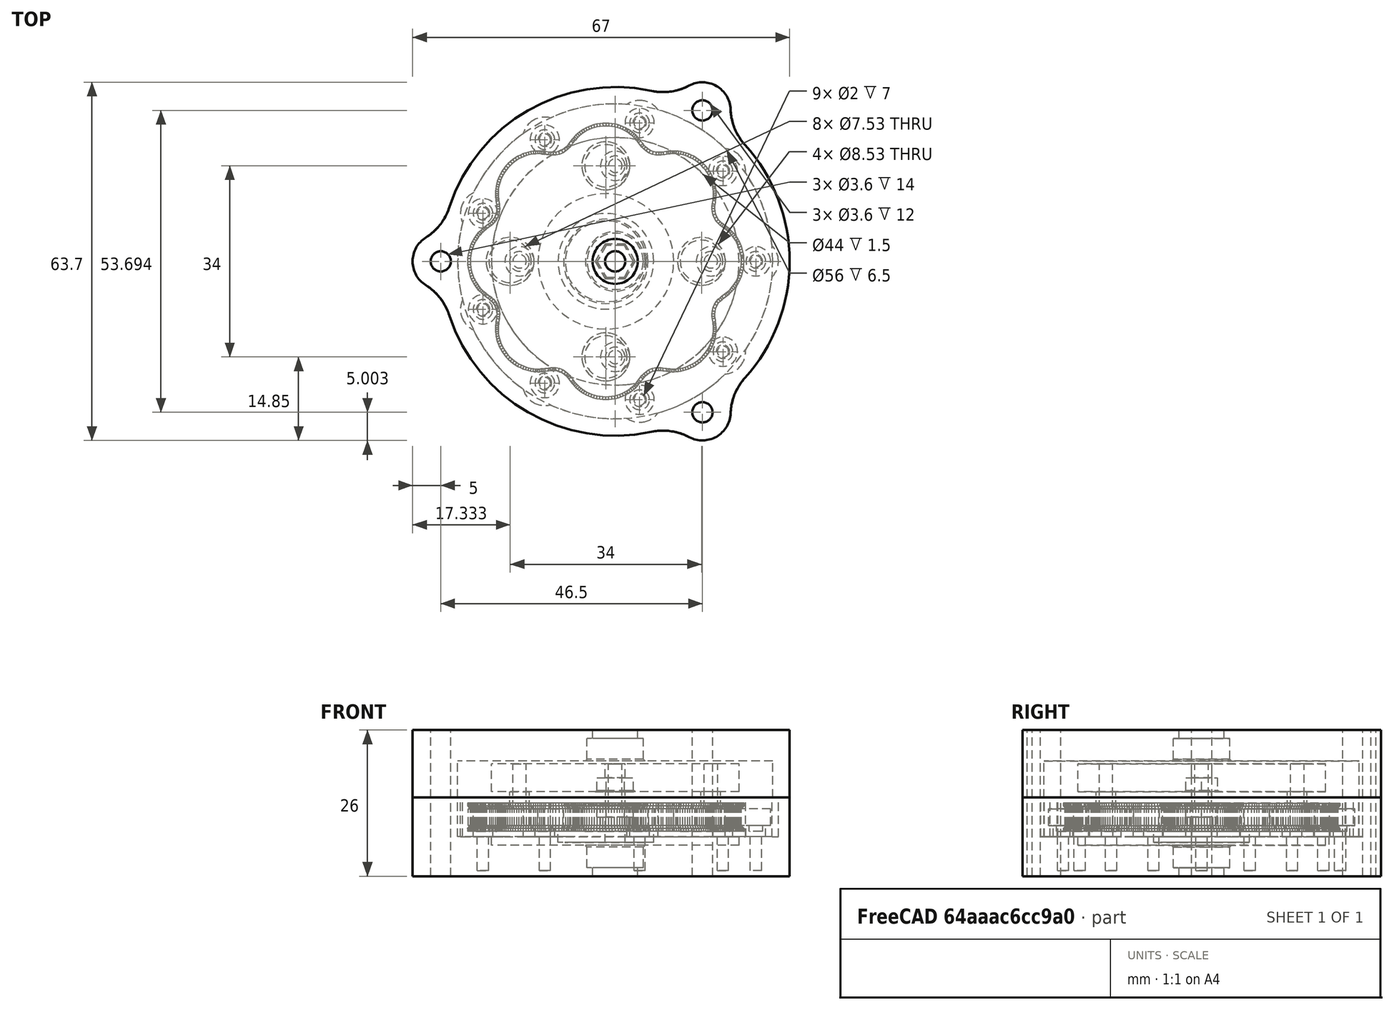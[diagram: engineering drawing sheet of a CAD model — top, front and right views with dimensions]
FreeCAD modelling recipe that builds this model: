
FCSTD DOCUMENT  (FreeCAD 0.19R24291 (Git))
Label: gearbox
License: All rights reserved
LicenseURL: http://en.wikipedia.org/wiki/All_rights_reserved
objects: Part::Feature×43, Part::Cylinder×24, Part::MultiFuse×20, Part::Cut×13, Part::Chamfer×4, Part::Box×2, Part::Fillet×2
note: 108 computed .brp shape members not serialized (recipe doc carries the construction recipe); baked Part::Feature solids carry a one-line shape summary decoded from their .brp

FEATURE [Part::Cylinder] Cylinder
  Angle = 360
  AttacherType = Attacher::AttachEngine3D
  Height = 7
  Placement = pos=(-1.6666,0,-3) rot=(0,0,1;0rad)
  Radius = 7.5
FEATURE [Part::Cylinder] Cylinder036  label="M3"
  Angle = 360
  AttacherType = Attacher::AttachEngine3D
  Height = 16
  Placement = pos=(0,0,-9) rot=(0,0,1;0rad)
  Radius = 1.8
FEATURE [Part::Cylinder] Cylinder038
  Angle = 360
  AttacherType = Attacher::AttachEngine3D
  Height = 2
  Placement = pos=(-1.66666,0,-3) rot=(0,0,1;0rad)
  Radius = 8.5
FEATURE [Part::Cylinder] Cylinder039  label="m2-tap-a"
  Angle = 360
  AttacherType = Attacher::AttachEngine3D
  Height = 30
  Placement = pos=(25,0,-1) rot=(0,0,1;0rad)
  Radius = 1.2
FEATURE [Part::Cylinder] Cylinder039009  label="m2-tap-a001"
  Angle = 360
  AttacherType = Attacher::AttachEngine3D
  Height = 30
  Placement = pos=(17,0,-8) rot=(0,0,1;0rad)
  Radius = 1.2
FEATURE [Part::Feature] Cylinder039009001
  Placement = pos=(1.9e-15,17,-8) rot=(0,0,1;1.5708rad)
  shape: bbox 2.4 x 2.4 x 30 mm, 3 faces (baked)
FEATURE [Part::Feature] Cylinder039009002
  Placement = pos=(-17,2e-15,-8) rot=(0,0,1;3.14159rad)
  shape: bbox 2.4 x 2.4 x 30 mm, 3 faces (baked)
FEATURE [Part::Feature] Cylinder039009003
  Placement = pos=(-4e-15,-17,-8) rot=(0,0,-1;1.5708rad)
  shape: bbox 2.4 x 2.4 x 30 mm, 3 faces (baked)
FEATURE [Part::MultiFuse] Fusion003  label="roller-m2-taps"
  Shapes = -> [Cylinder039009,Cylinder039009001,Cylinder039009002,Cylinder039009003]
FEATURE [Part::Feature] Shape  label="cycloid"
  Placement = pos=(-1.66667,0,0) rot=(0,0,1;0rad)
  shape: bbox 49.13 x 49.13 x 5 mm, 1823 faces (baked)
FEATURE [Part::Feature] Shape002  label="rollers"
  shape: bbox 39.2 x 39.2 x 3 mm, 12 faces, 4 solids (baked)
FEATURE [Part::Feature] Shape003  label="bearings"
  shape: bbox 53.69 x 54.44 x 3 mm, 27 faces, 9 solids (baked)
FEATURE [Part::Cylinder] Cylinder039009004
  Angle = 360
  AttacherType = Attacher::AttachEngine3D
  Height = 2
  Placement = pos=(25,0,-2) rot=(0,0,1;0rad)
  Radius = 1.75
FEATURE [Part::Feature] Cylinder039009004001
  Placement = pos=(19.1511,16.0697,-2) rot=(0,0,1;0.698132rad)
  shape: bbox 3.5 x 3.5 x 2 mm, 3 faces (baked)
FEATURE [Part::Feature] Cylinder039009004002
  Placement = pos=(4.3412,24.6202,-2) rot=(0,0,1;1.39626rad)
  shape: bbox 3.5 x 3.5 x 2 mm, 3 faces (baked)
FEATURE [Part::Feature] Cylinder039009004003
  Placement = pos=(-12.5,21.6506,-2) rot=(0,0,1;2.0944rad)
  shape: bbox 3.5 x 3.5 x 2 mm, 3 faces (baked)
FEATURE [Part::Feature] Cylinder039009004004
  Placement = pos=(-23.4923,8.5505,-2) rot=(0,0,1;2.79253rad)
  shape: bbox 3.5 x 3.5 x 2 mm, 3 faces (baked)
FEATURE [Part::Feature] Cylinder039009004005
  Placement = pos=(-23.4923,-8.5505,-2) rot=(0,0,1;3.49066rad)
  shape: bbox 3.5 x 3.5 x 2 mm, 3 faces (baked)
FEATURE [Part::Feature] Cylinder039009004006
  Placement = pos=(-12.5,-21.6506,-2) rot=(0,0,1;4.18879rad)
  shape: bbox 3.5 x 3.5 x 2 mm, 3 faces (baked)
FEATURE [Part::Feature] Cylinder039009004007
  Placement = pos=(4.3412,-24.6202,-2) rot=(0,0,-1;1.39626rad)
  shape: bbox 3.5 x 3.5 x 2 mm, 3 faces (baked)
FEATURE [Part::Feature] Cylinder039009004008
  Placement = pos=(19.1511,-16.0697,-2) rot=(0,0,-1;0.698132rad)
  shape: bbox 3.5 x 3.5 x 2 mm, 3 faces (baked)
FEATURE [Part::MultiFuse] Fusion004  label="bearing supports"
  Shapes = -> [Cylinder039009004,Cylinder039009004001,Cylinder039009004002,Cylinder039009004003,Cylinder039009004004,Cylinder039009004005,Cylinder039009004006,Cylinder039009004007,Cylinder039009004008]
FEATURE [Part::Cylinder] Cylinder039009004009
  Angle = 360
  AttacherType = Attacher::AttachEngine3D
  Height = 13
  Placement = pos=(25,0,-1) rot=(0,0,1;0rad)
  Radius = 4
FEATURE [Part::Feature] Cylinder039009004009001
  Placement = pos=(19.1511,16.0697,-1) rot=(0,0,1;0.698132rad)
  shape: bbox 8 x 8 x 13 mm, 3 faces (baked)
FEATURE [Part::Feature] Cylinder039009004009002
  Placement = pos=(4.3412,24.6202,-1) rot=(0,0,1;1.39626rad)
  shape: bbox 8 x 8 x 13 mm, 3 faces (baked)
FEATURE [Part::Feature] Cylinder039009004009003
  Placement = pos=(-12.5,21.6506,-1) rot=(0,0,1;2.0944rad)
  shape: bbox 8 x 8 x 13 mm, 3 faces (baked)
FEATURE [Part::Feature] Cylinder039009004009004
  Placement = pos=(-23.4923,8.5505,-1) rot=(0,0,1;2.79253rad)
  shape: bbox 8 x 8 x 13 mm, 3 faces (baked)
FEATURE [Part::Feature] Cylinder039009004009005
  Placement = pos=(-23.4923,-8.5505,-1) rot=(0,0,1;3.49066rad)
  shape: bbox 8 x 8 x 13 mm, 3 faces (baked)
FEATURE [Part::Feature] Cylinder039009004009006
  Placement = pos=(-12.5,-21.6506,-1) rot=(0,0,1;4.18879rad)
  shape: bbox 8 x 8 x 13 mm, 3 faces (baked)
FEATURE [Part::Feature] Cylinder039009004009007
  Placement = pos=(4.3412,-24.6202,-1) rot=(0,0,-1;1.39626rad)
  shape: bbox 8 x 8 x 13 mm, 3 faces (baked)
FEATURE [Part::Feature] Cylinder039009004009008
  Placement = pos=(19.1511,-16.0697,-1) rot=(0,0,-1;0.698132rad)
  shape: bbox 8 x 8 x 13 mm, 3 faces (baked)
FEATURE [Part::MultiFuse] Fusion005  label="bearing-cavities"
  Placement = pos=(0,0,-1) rot=(0,0,1;0rad)
  Shapes = -> [Cylinder039009004009,Cylinder039009004009001,Cylinder039009004009002,Cylinder039009004009003,Cylinder039009004009004,Cylinder039009004009005,Cylinder039009004009006,Cylinder039009004009007,Cylinder039009004009008]
FEATURE [Part::Cylinder] Cylinder039009004009009  label="case-0"
  Angle = 360
  AttacherType = Attacher::AttachEngine3D
  Height = 14
  Placement = pos=(0,0,-9) rot=(0,0,1;0rad)
  Radius = 31
FEATURE [Part::Cylinder] Cylinder039009004009010  label="case-hole-1"
  Angle = 360
  AttacherType = Attacher::AttachEngine3D
  Height = 28
  Placement = pos=(0,0,-2) rot=(0,0,1;0rad)
  Radius = 28
FEATURE [Part::Cylinder] Cylinder039009004009011  label="case-hole-2"
  Angle = 360
  AttacherType = Attacher::AttachEngine3D
  Height = 5
  Placement = pos=(0,0,-3.5) rot=(0,0,1;0rad)
  Radius = 22
FEATURE [Part::Cylinder] Cylinder039009004009012  label="output-1"
  Angle = 360
  AttacherType = Attacher::AttachEngine3D
  Height = 5
  Placement = pos=(0,0,6) rot=(0,0,1;0rad)
  Radius = 22
FEATURE [Part::Cylinder] Cylinder039009004009013
  Angle = 360
  AttacherType = Attacher::AttachEngine3D
  Height = 4
  Placement = pos=(17,0,3) rot=(0,0,1;0rad)
  Radius = 1.75
FEATURE [Part::Feature] Cylinder039009004009013001
  Placement = pos=(1.9e-15,17,3) rot=(0,0,1;1.5708rad)
  shape: bbox 3.5 x 3.5 x 4 mm, 3 faces (baked)
FEATURE [Part::Feature] Cylinder039009004009013002
  Placement = pos=(-17,2e-15,3) rot=(0,0,1;3.14159rad)
  shape: bbox 3.5 x 3.5 x 4 mm, 3 faces (baked)
FEATURE [Part::Feature] Cylinder039009004009013003
  Placement = pos=(-4e-15,-17,3) rot=(0,0,-1;1.5708rad)
  shape: bbox 3.5 x 3.5 x 4 mm, 3 faces (baked)
FEATURE [Part::MultiFuse] Fusion008  label="roller-supports"
  Shapes = -> [Cylinder039009004009013,Cylinder039009004009013001,Cylinder039009004009013002,Cylinder039009004009013003]
FEATURE [Part::MultiFuse] Fusion009  label="output-2"
  Shapes = -> [Cylinder039009004009012,Fusion008]
FEATURE [Part::Cut] Cut004  label="output-3"
  Base = -> Fusion009
  Tool = -> Fusion003
FEATURE [Part::Feature] M3_Nut_Hole
  Placement = pos=(0,0,2.5) rot=(0,0,1;0rad)
  shape: bbox 6.466 x 5.6 x 6 mm, 8 faces (baked)
FEATURE [Part::Cylinder] Cylinder039009004009013004
  Angle = 360
  AttacherType = Attacher::AttachEngine3D
  Height = 23
  Placement = pos=(0,0,3) rot=(0,0,1;0rad)
  Radius = 1.8
FEATURE [Part::MultiFuse] Fusion010  label="output-screw"
  Shapes = -> [Cylinder039009004009013004,M3_Nut_Hole]
FEATURE [Part::Cut] Cut005  label="output-4"
  Base = -> Cut004
  Tool = -> Fusion010
FEATURE [Part::Chamfer] Chamfer002  label="output"
  Base = -> Cut005
  Edges = 6 edges r=0.3: [Edge11,Edge12,Edge13,Edge14,Edge15,Edge16]
FEATURE [Part::Cylinder] Cylinder039009004009013005  label="case-hole-003"
  Angle = 360
  AttacherType = Attacher::AttachEngine3D
  Height = 13.5
  Placement = pos=(0,0,-2) rot=(0,0,1;0rad)
  Radius = 28
FEATURE [Part::Cylinder] Cylinder039009004009013006  label="case-005"
  Angle = 360
  AttacherType = Attacher::AttachEngine3D
  Height = 12
  Placement = pos=(0,0,5) rot=(0,0,1;0rad)
  Radius = 31
FEATURE [Part::Cut] Cut006  label="top-1"
  Base = -> Cylinder039009004009013006
  Tool = -> Cylinder039009004009013005
FEATURE [Part::Cylinder] Cylinder039009004009013007  label="10mm-bearing"
  Angle = 360
  AttacherType = Attacher::AttachEngine3D
  Height = 4
  Placement = pos=(0,0,11.5) rot=(0,0,1;0rad)
  Radius = 5
FEATURE [Part::Cylinder] Cylinder039009004009013008  label="output-hole"
  Angle = 360
  AttacherType = Attacher::AttachEngine3D
  Height = 10
  Placement = pos=(0,0,13) rot=(0,0,1;0rad)
  Radius = 4
FEATURE [Part::MultiFuse] Fusion011  label="output-hole-2"
  Shapes = -> [Cylinder039009004009013007,Cylinder039009004009013008]
FEATURE [Part::Cut] Cut007  label="top-3"
  Base = -> Cut006
  Tool = -> Fusion011
FEATURE [Part::Cylinder] Cylinder039009004009013009  label="case-screw-1"
  Angle = 360
  AttacherType = Attacher::AttachEngine3D
  Height = 14
  Placement = pos=(-31,0,-9) rot=(0,0,1;0rad)
  Radius = 5
FEATURE [Part::Cylinder] Cylinder039009004009013010  label="top-screw-1"
  Angle = 360
  AttacherType = Attacher::AttachEngine3D
  Height = 12
  Placement = pos=(-31,0,5) rot=(0,0,1;0rad)
  Radius = 5
FEATURE [Part::Box] Box  label="Cube"
  AttacherType = Attacher::AttachEngine3D
  Height = 56
  Length = 16
  Placement = pos=(-29,-8,-26) rot=(0,0,1;0rad)
  Width = 16
FEATURE [Part::Box] Box001  label="Cube001"
  AttacherType = Attacher::AttachEngine3D
  Height = 56
  Length = 16
  Placement = pos=(-29,-8,-26) rot=(0,0,1;0rad)
  Width = 16
FEATURE [Part::Cut] Cut008  label="case-boss-1"
  Base = -> Cylinder039009004009013009
  Tool = -> Box
FEATURE [Part::Cut] Cut009  label="top-screw-2"
  Base = -> Cylinder039009004009013010
  Tool = -> Box001
FEATURE [Part::Cylinder] Cylinder039009004009013011  label="case-screw-M3"
  Angle = 360
  AttacherType = Attacher::AttachEngine3D
  Height = 47
  Placement = pos=(-31,0,-26) rot=(0,0,1;0rad)
  Radius = 1.8
FEATURE [Part::Cylinder] Cylinder039009004009013012  label="Top-screw-clear-1"
  Angle = 360
  AttacherType = Attacher::AttachEngine3D
  Height = 47
  Placement = pos=(-31,0,-26) rot=(0,0,1;0rad)
  Radius = 1.8
FEATURE [Part::Feature] Cut009001
  Placement = pos=(0,0,0) rot=(0,0,1;2.0944rad)
  shape: bbox 9.969 x 9.023 x 12 mm, 4 faces (baked)
FEATURE [Part::Feature] Cut009002
  Placement = pos=(0,0,0) rot=(0,0,1;4.18879rad)
  shape: bbox 9.969 x 9.023 x 12 mm, 4 faces (baked)
FEATURE [Part::Feature] Cylinder039009004009013012001
  Placement = pos=(15.5,-26.8468,-26) rot=(0,0,1;2.0944rad)
  shape: bbox 3.6 x 3.6 x 47 mm, 3 faces (baked)
FEATURE [Part::Feature] Cylinder039009004009013012002
  Placement = pos=(15.5,26.8468,-26) rot=(0,0,1;4.18879rad)
  shape: bbox 3.6 x 3.6 x 47 mm, 3 faces (baked)
FEATURE [Part::MultiFuse] Fusion015  label="top-screw-clears"
  Shapes = -> [Cylinder039009004009013012,Cylinder039009004009013012001,Cylinder039009004009013012002]
FEATURE [Part::MultiFuse] Fusion016  label="top-screws"
  Shapes = -> [Cut009,Cut009001,Cut009002]
FEATURE [Part::MultiFuse] Fusion017  label="top-4"
  Shapes = -> [Cut007,Fusion016]
FEATURE [Part::Cut] Cut009006  label="top-5"
  Base = -> Fusion017
  Tool = -> Fusion015
FEATURE [Part::Fillet] Fillet001  label="top-6"
  Base = -> Cut009006
  Edges = 6 edges r=10: [Edge3,Edge6,Edge22,Edge36,Edge42,Edge47]
FEATURE [Part::Feature] M3_Nut_Hole001
  Placement = pos=(0,0,1.5) rot=(0,0,1;0rad)
  shape: bbox 6.466 x 5.6 x 6 mm, 8 faces (baked)
FEATURE [Part::MultiFuse] Fusion  label="M3-hex"
  Shapes = -> [Cylinder036,M3_Nut_Hole001]
FEATURE [Part::MultiFuse] Fusion019  label="drive-1"
  Shapes = -> [Cylinder,Cylinder038]
FEATURE [Part::Cut] Cut  label="drive-2"
  Base = -> Fusion019
  Tool = -> Fusion
FEATURE [Part::Chamfer] Chamfer  label="drive"
  Base = -> Cut
  Edges = 7 edges r=0.3: [Edge3,Edge5,Edge6,Edge7,Edge8,Edge9,Edge10]
FEATURE [Part::MultiFuse] Fusion020  label="case-hole"
  Shapes = -> [Cylinder039009004009010,Cylinder039009004009011]
FEATURE [Part::Cut] Cut009007  label="case-1"
  Base = -> Cylinder039009004009009
  Tool = -> Fusion020
FEATURE [Part::Cut] Cut009008  label="case-3"
  Base = -> Cut009007
  Tool = -> Fusion005
FEATURE [Part::MultiFuse] Fusion021  label="case-4"
  Shapes = -> [Cut009008,Fusion004]
FEATURE [Part::Cylinder] Cylinder039009004009013012003  label="m2-tap-a002"
  Angle = 360
  AttacherType = Attacher::AttachEngine3D
  Height = 30
  Placement = pos=(25,0,-8) rot=(0,0,1;0rad)
  Radius = 1
FEATURE [Part::MultiFuse] Fusion022  label="M2-tap"
  Shapes = -> [Cylinder039,Cylinder039009004009013012003]
FEATURE [Part::Feature] Fusion022001
  Placement = pos=(0,0,0) rot=(0,0,1;0.698132rad)
  shape: bbox 2.4 x 2.4 x 37 mm, 5 faces (baked)
FEATURE [Part::Feature] Fusion022002
  Placement = pos=(0,0,0) rot=(0,0,1;1.39626rad)
  shape: bbox 2.4 x 2.4 x 37 mm, 5 faces (baked)
FEATURE [Part::Feature] Fusion022003
  Placement = pos=(0,0,0) rot=(0,0,1;2.0944rad)
  shape: bbox 2.4 x 2.4 x 37 mm, 5 faces (baked)
FEATURE [Part::Feature] Fusion022004
  Placement = pos=(0,0,0) rot=(0,0,1;2.79253rad)
  shape: bbox 2.4 x 2.4 x 37 mm, 5 faces (baked)
FEATURE [Part::Feature] Fusion022005
  Placement = pos=(0,0,0) rot=(0,0,1;3.49066rad)
  shape: bbox 2.4 x 2.4 x 37 mm, 5 faces (baked)
FEATURE [Part::Feature] Fusion022006
  Placement = pos=(0,0,0) rot=(0,0,1;4.18879rad)
  shape: bbox 2.4 x 2.4 x 37 mm, 5 faces (baked)
FEATURE [Part::Feature] Fusion022007
  Placement = pos=(0,0,0) rot=(0,0,-1;1.39626rad)
  shape: bbox 2.4 x 2.4 x 37 mm, 5 faces (baked)
FEATURE [Part::Feature] Fusion022008
  Placement = pos=(0,0,0) rot=(0,0,-1;0.698132rad)
  shape: bbox 2.4 x 2.4 x 37 mm, 5 faces (baked)
FEATURE [Part::MultiFuse] Fusion022009  label="M2-taps"
  Shapes = -> [Fusion022,Fusion022001,Fusion022002,Fusion022003,Fusion022004,Fusion022005,Fusion022006,Fusion022007,Fusion022008]
FEATURE [Part::Cut] Cut009009  label="case-5"
  Base = -> Fusion021
  Tool = -> Fusion022009
FEATURE [Part::Cylinder] Cylinder039009004009013012004  label="10mm-bearing001"
  Angle = 360
  AttacherType = Attacher::AttachEngine3D
  Height = 4
  Placement = pos=(0,0,-7.5) rot=(0,0,1;0rad)
  Radius = 5
FEATURE [Part::Cylinder] Cylinder039009004009013012005  label="10mm-bearing002"
  Angle = 360
  AttacherType = Attacher::AttachEngine3D
  Height = 7
  Placement = pos=(0,0,-12.5) rot=(0,0,1;0rad)
  Radius = 4
FEATURE [Part::MultiFuse] Fusion022010  label="case-bearing-hole"
  Shapes = -> [Cylinder039009004009013012004,Cylinder039009004009013012005]
FEATURE [Part::Cut] Cut009010  label="case-6"
  Base = -> Cut009009
  Tool = -> Fusion022010
FEATURE [Part::Feature] Cut008001
  Placement = pos=(0,0,0) rot=(0,0,1;2.0944rad)
  shape: bbox 9.969 x 9.023 x 14 mm, 4 faces (baked)
FEATURE [Part::Feature] Cut008002
  Placement = pos=(0,0,0) rot=(0,0,1;4.18879rad)
  shape: bbox 9.969 x 9.023 x 14 mm, 4 faces (baked)
FEATURE [Part::MultiFuse] Fusion022011  label="case-bosses"
  Shapes = -> [Cut008,Cut008001,Cut008002]
FEATURE [Part::MultiFuse] Fusion022012  label="case-7"
  Shapes = -> [Cut009010,Fusion022011]
FEATURE [Part::Feature] Cylinder039009004009013011001
  Placement = pos=(15.5,-26.8468,-26) rot=(0,0,1;2.0944rad)
  shape: bbox 3.6 x 3.6 x 47 mm, 3 faces (baked)
FEATURE [Part::Feature] Cylinder039009004009013011002
  Placement = pos=(15.5,26.8468,-26) rot=(0,0,1;4.18879rad)
  shape: bbox 3.6 x 3.6 x 47 mm, 3 faces (baked)
FEATURE [Part::MultiFuse] Fusion022013  label="case-M3-screws"
  Shapes = -> [Cylinder039009004009013011,Cylinder039009004009013011001,Cylinder039009004009013011002]
FEATURE [Part::Fillet] Fillet  label="case-8"
  Base = -> Fusion022012
  Edges = 6 edges r=10: [Edge3,Edge6,Edge22,Edge62,Edge65,Edge67]
FEATURE [Part::Cut] Cut009011  label="case-9"
  Base = -> Fillet
  Tool = -> Fusion022013
FEATURE [Part::Chamfer] Chamfer003  label="case"
  Base = -> Cut009011
  Edges = 1 edges r=0.3: [Edge225]
FEATURE [Part::Chamfer] Chamfer004  label="top"
  Base = -> Fillet001
  Edges = 1 edges r=0.3: [Edge109]
